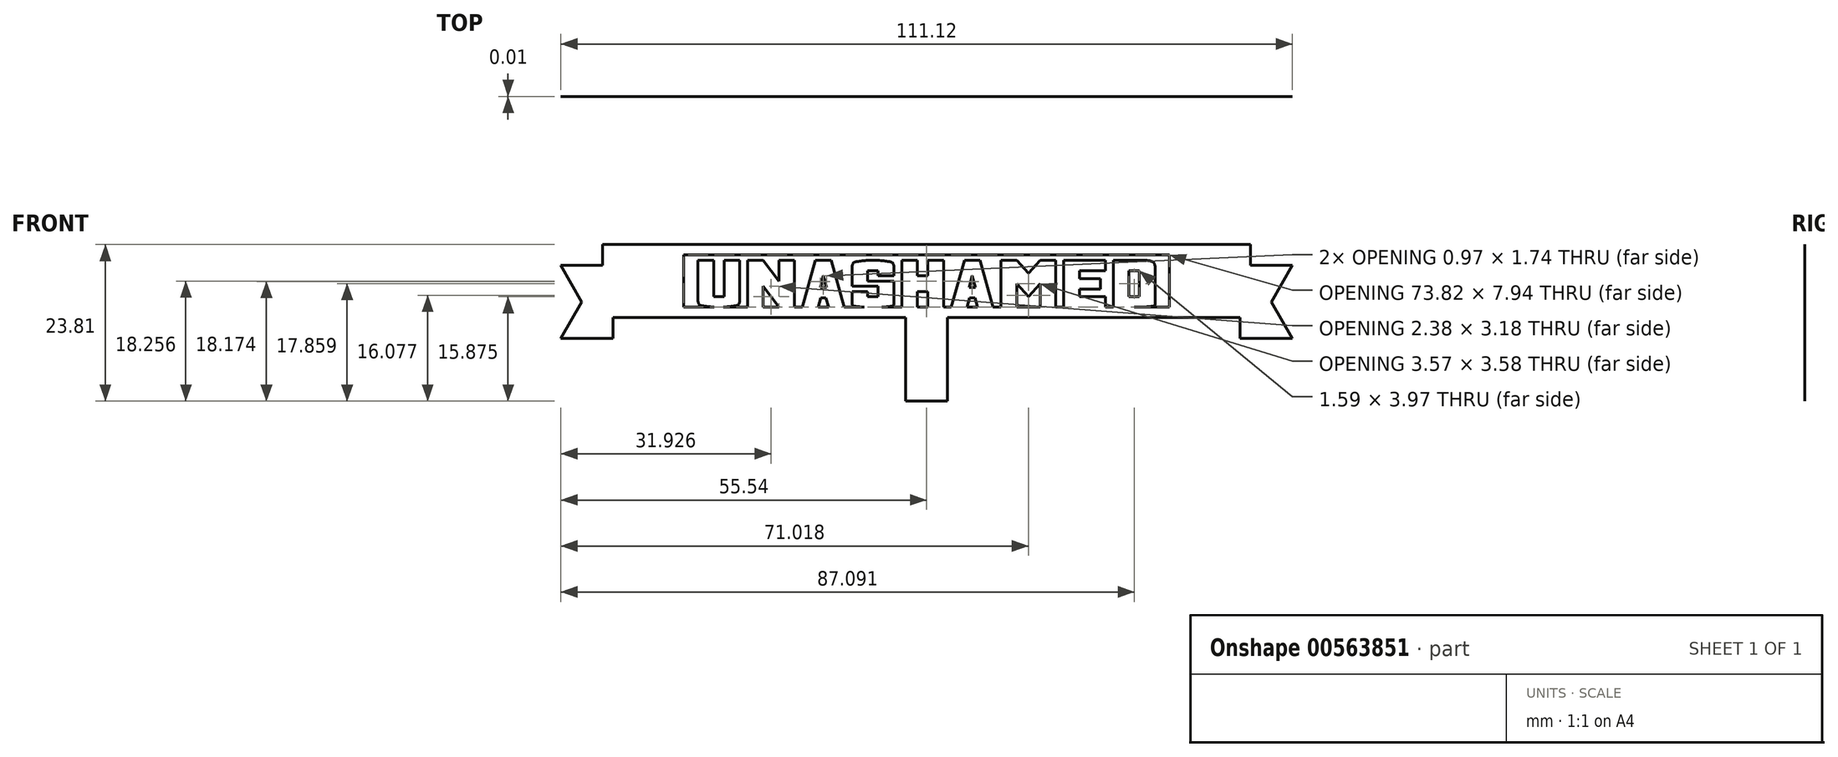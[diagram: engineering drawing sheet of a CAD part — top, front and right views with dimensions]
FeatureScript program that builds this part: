
annotation { "Feature Type Name" : "Feature", "Feature Type Description" : "" }
export const myFeature = defineFeature(function(context is Context, id is Id, definition is map)
    precondition{}
    {
        {
            var Q0;
            Q0=qCreatedBy(makeId("Front.planeOp"),FACE);
            var sketch = newSketch(context, id + "F0", { "sketchPlane" : qUnion([Q0])});
            skLineSegment(sketch, "E0.bottom", {"start": v(55.58, 34.93) * mm, "end": v(-55.54, 34.93) * mm});
            skLineSegment(sketch, "E0.top", {"start": v(55.58, -34.92) * mm, "end": v(-55.54, -34.93) * mm});
            skLineSegment(sketch, "E0.left", {"start": v(55.58, 34.93) * mm, "end": v(55.58, -34.92) * mm});
            skLineSegment(sketch, "E0.right", {"start": v(-55.54, 34.93) * mm, "end": v(-55.54, -34.93) * mm});
            skLineSegment(sketch, "E1", {"start": v(-47.6, -31.75) * mm, "end": v(47.64, -31.75) * mm});
            skLineSegment(sketch, "E2", {"start": v(-47.6, -31.75) * mm, "end": v(-47.6, -34.93) * mm});
            skLineSegment(sketch, "E3", {"start": v(-47.6, -34.93) * mm, "end": v(-55.54, -34.93) * mm});
            skLineSegment(sketch, "E4", {"start": v(-55.54, -34.93) * mm, "end": v(-52.37, -29.37) * mm});
            skLineSegment(sketch, "E5", {"start": v(-52.37, -29.37) * mm, "end": v(-55.54, -23.81) * mm});
            skLineSegment(sketch, "E6", {"start": v(-55.54, -23.81) * mm, "end": v(-49.2, -23.81) * mm});
            skLineSegment(sketch, "E7.bottom", {"start": v(36.9, -22.23) * mm, "end": v(-36.9, -22.23) * mm});
            skLineSegment(sketch, "E7.top", {"start": v(36.9, -30.16) * mm, "end": v(-36.9, -30.16) * mm});
            skLineSegment(sketch, "E7.left", {"start": v(36.9, -22.23) * mm, "end": v(36.9, -30.16) * mm});
            skLineSegment(sketch, "E7.right", {"start": v(-36.9, -22.22) * mm, "end": v(-36.9, -30.16) * mm});
            skPoint(sketch, "E7.middle", {"position": v(0, -26.2) * mm});
            skLineSegment(sketch, "E8", {"start": v(-34.73, -30.16) * mm, "end": v(-34.73, -23.02) * mm});
            skLineSegment(sketch, "E9", {"start": v(-34.73, -23.02) * mm, "end": v(-32.35, -23.02) * mm});
            skLineSegment(sketch, "E10", {"start": v(-32.35, -23.02) * mm, "end": v(-32.35, -28.57) * mm});
            skLineSegment(sketch, "E11", {"start": v(-30.76, -28.57) * mm, "end": v(-30.76, -23.02) * mm});
            skLineSegment(sketch, "E12", {"start": v(-30.76, -23.02) * mm, "end": v(-28.38, -23.02) * mm});
            skLineSegment(sketch, "E13", {"start": v(-28.38, -23.02) * mm, "end": v(-28.38, -30.16) * mm});
            skLineSegment(sketch, "E14", {"start": v(-28.38, -30.16) * mm, "end": v(-34.73, -30.16) * mm});
            skLineSegment(sketch, "E15", {"start": v(28.38, -30.16) * mm, "end": v(28.38, -23.02) * mm});
            skLineSegment(sketch, "E16", {"start": v(28.38, -23.02) * mm, "end": v(34.73, -23.02) * mm});
            skLineSegment(sketch, "E17", {"start": v(34.73, -23.02) * mm, "end": v(34.73, -30.16) * mm});
            skLineSegment(sketch, "E18", {"start": v(34.73, -30.16) * mm, "end": v(28.38, -30.16) * mm});
            skLineSegment(sketch, "E19", {"start": v(30.76, -28.57) * mm, "end": v(30.76, -24.6) * mm});
            skLineSegment(sketch, "E20", {"start": v(30.76, -24.6) * mm, "end": v(32.35, -24.6) * mm});
            skLineSegment(sketch, "E21", {"start": v(32.35, -24.6) * mm, "end": v(32.35, -28.57) * mm});
            skLineSegment(sketch, "E22", {"start": v(32.35, -28.58) * mm, "end": v(30.76, -28.58) * mm});
            skLineSegment(sketch, "E23", {"start": v(-49.2, -20.64) * mm, "end": v(49.23, -20.64) * mm});
            skArc(sketch, "E24", {"start": v(-48.44, 34.93) * mm, "mid": v(0, 9.84) * mm, "end": v(48.44, 34.93) * mm});
            skLineSegment(sketch, "E25", {"start": v(47.64, -31.75) * mm, "end": v(47.64, -34.92) * mm});
            skLineSegment(sketch, "E26", {"start": v(47.64, -34.92) * mm, "end": v(55.58, -34.92) * mm});
            skLineSegment(sketch, "E27", {"start": v(55.58, -34.92) * mm, "end": v(52.4, -29.37) * mm});
            skLineSegment(sketch, "E28", {"start": v(52.4, -29.37) * mm, "end": v(55.58, -23.81) * mm});
            skLineSegment(sketch, "E29", {"start": v(55.58, -23.81) * mm, "end": v(49.23, -23.81) * mm});
            skLineSegment(sketch, "E30", {"start": v(49.23, -23.82) * mm, "end": v(49.23, -23.81) * mm});
            skLineSegment(sketch, "E31", {"start": v(49.23, -23.81) * mm, "end": v(49.23, -20.64) * mm});
            skLineSegment(sketch, "E32", {"start": v(-3.16, -31.75) * mm, "end": v(-3.16, -44.45) * mm});
            skLineSegment(sketch, "E33", {"start": v(-3.16, -44.45) * mm, "end": v(3.2, -44.45) * mm});
            skLineSegment(sketch, "E34", {"start": v(3.2, -44.45) * mm, "end": v(3.2, -31.75) * mm});
            skLineSegment(sketch, "E35", {"start": v(-49.2, -23.81) * mm, "end": v(-49.2, -20.64) * mm});
            skLineSegment(sketch, "E36", {"start": v(-32.35, -28.58) * mm, "end": v(-30.76, -28.58) * mm});
            skLineSegment(sketch, "E37", {"start": v(-27.19, -30.16) * mm, "end": v(-27.19, -23.02) * mm});
            skLineSegment(sketch, "E38", {"start": v(-27.19, -23.02) * mm, "end": v(-24.8, -23.02) * mm});
            skLineSegment(sketch, "E39", {"start": v(-24.8, -23.02) * mm, "end": v(-22.42, -26.2) * mm});
            skLineSegment(sketch, "E40", {"start": v(-22.42, -26.2) * mm, "end": v(-22.42, -23.02) * mm});
            skLineSegment(sketch, "E41", {"start": v(-22.42, -23.02) * mm, "end": v(-20.04, -23.02) * mm});
            skLineSegment(sketch, "E42", {"start": v(-20.04, -23.02) * mm, "end": v(-20.04, -30.16) * mm});
            skLineSegment(sketch, "E43", {"start": v(-20.04, -30.16) * mm, "end": v(-22.42, -30.16) * mm});
            skLineSegment(sketch, "E44", {"start": v(-22.42, -30.16) * mm, "end": v(-24.8, -26.99) * mm});
            skLineSegment(sketch, "E45", {"start": v(-24.8, -26.99) * mm, "end": v(-24.8, -30.16) * mm});
            skLineSegment(sketch, "E46", {"start": v(-24.8, -30.16) * mm, "end": v(-27.19, -30.16) * mm});
            skLineSegment(sketch, "E47", {"start": v(-18.85, -30.16) * mm, "end": v(-16.87, -23.02) * mm});
            skLineSegment(sketch, "E48", {"start": v(-16.87, -23.02) * mm, "end": v(-14.49, -23.02) * mm});
            skLineSegment(sketch, "E49", {"start": v(-14.49, -23.02) * mm, "end": v(-12.5, -30.16) * mm});
            skLineSegment(sketch, "E50", {"start": v(-12.5, -30.16) * mm, "end": v(-14.88, -30.16) * mm});
            skLineSegment(sketch, "E51", {"start": v(-14.88, -30.16) * mm, "end": v(-15.28, -28.73) * mm});
            skLineSegment(sketch, "E52", {"start": v(-15.28, -28.73) * mm, "end": v(-16.07, -28.73) * mm});
            skLineSegment(sketch, "E53", {"start": v(-16.07, -28.73) * mm, "end": v(-16.47, -30.16) * mm});
            skLineSegment(sketch, "E54", {"start": v(-16.47, -30.16) * mm, "end": v(-18.85, -30.16) * mm});
            skPoint(sketch, "E55", {"position": v(-15.68, -23.02) * mm});
            skLineSegment(sketch, "E56", {"start": v(-15.68, -25.4) * mm, "end": v(-16.16, -27.15) * mm});
            skLineSegment(sketch, "E57", {"start": v(-16.16, -27.15) * mm, "end": v(-15.2, -27.15) * mm});
            skLineSegment(sketch, "E58", {"start": v(-15.2, -27.15) * mm, "end": v(-15.68, -25.4) * mm});
            skLineSegment(sketch, "E59", {"start": v(-3.77, -30.16) * mm, "end": v(-3.77, -23.02) * mm});
            skLineSegment(sketch, "E60", {"start": v(-3.77, -23.02) * mm, "end": v(-1.39, -23.02) * mm});
            skLineSegment(sketch, "E61", {"start": v(-1.39, -23.02) * mm, "end": v(-1.39, -25.4) * mm});
            skLineSegment(sketch, "E62", {"start": v(-1.39, -25.4) * mm, "end": v(0.2, -25.4) * mm});
            skLineSegment(sketch, "E63", {"start": v(0.2, -25.4) * mm, "end": v(0.2, -23.02) * mm});
            skLineSegment(sketch, "E64", {"start": v(0.2, -23.02) * mm, "end": v(2.58, -23.02) * mm});
            skLineSegment(sketch, "E65", {"start": v(2.58, -23.02) * mm, "end": v(2.58, -30.16) * mm});
            skLineSegment(sketch, "E66", {"start": v(2.58, -30.16) * mm, "end": v(0.2, -30.16) * mm});
            skLineSegment(sketch, "E67", {"start": v(0.2, -30.16) * mm, "end": v(0.2, -27.78) * mm});
            skLineSegment(sketch, "E68", {"start": v(0.2, -27.78) * mm, "end": v(-1.39, -27.78) * mm});
            skLineSegment(sketch, "E69", {"start": v(-1.39, -27.78) * mm, "end": v(-1.39, -30.16) * mm});
            skLineSegment(sketch, "E70", {"start": v(-1.39, -30.16) * mm, "end": v(-3.77, -30.16) * mm});
            skLineSegment(sketch, "E71", {"start": v(3.77, -30.16) * mm, "end": v(5.75, -23.02) * mm});
            skLineSegment(sketch, "E72", {"start": v(5.75, -23.02) * mm, "end": v(8.14, -23.02) * mm});
            skLineSegment(sketch, "E73", {"start": v(8.14, -23.02) * mm, "end": v(10.12, -30.16) * mm});
            skLineSegment(sketch, "E74", {"start": v(10.12, -30.16) * mm, "end": v(7.74, -30.16) * mm});
            skLineSegment(sketch, "E75", {"start": v(7.74, -30.16) * mm, "end": v(7.34, -28.73) * mm});
            skLineSegment(sketch, "E76", {"start": v(7.34, -28.73) * mm, "end": v(6.55, -28.73) * mm});
            skLineSegment(sketch, "E77", {"start": v(6.55, -28.73) * mm, "end": v(6.15, -30.16) * mm});
            skLineSegment(sketch, "E78", {"start": v(6.15, -30.16) * mm, "end": v(3.77, -30.16) * mm});
            skPoint(sketch, "E79", {"position": v(6.95, -23.02) * mm});
            skLineSegment(sketch, "E80", {"start": v(6.95, -25.4) * mm, "end": v(6.46, -27.15) * mm});
            skLineSegment(sketch, "E81", {"start": v(6.46, -27.15) * mm, "end": v(7.43, -27.15) * mm});
            skLineSegment(sketch, "E82", {"start": v(7.43, -27.15) * mm, "end": v(6.95, -25.4) * mm});
            skLineSegment(sketch, "E83", {"start": v(11.31, -30.16) * mm, "end": v(11.31, -23.02) * mm});
            skLineSegment(sketch, "E84", {"start": v(11.31, -23.02) * mm, "end": v(13.7, -23.02) * mm});
            skLineSegment(sketch, "E85", {"start": v(13.7, -23.02) * mm, "end": v(15.48, -25) * mm});
            skLineSegment(sketch, "E86", {"start": v(15.48, -25) * mm, "end": v(17.26, -23.02) * mm});
            skLineSegment(sketch, "E87", {"start": v(17.26, -23.02) * mm, "end": v(19.65, -23.02) * mm});
            skLineSegment(sketch, "E88", {"start": v(19.65, -23.02) * mm, "end": v(19.65, -30.16) * mm});
            skLineSegment(sketch, "E89", {"start": v(19.65, -30.16) * mm, "end": v(17.26, -30.16) * mm});
            skLineSegment(sketch, "E90", {"start": v(17.26, -30.16) * mm, "end": v(17.26, -26.58) * mm});
            skLineSegment(sketch, "E91", {"start": v(15.48, -28.57) * mm, "end": v(17.26, -26.58) * mm});
            skLineSegment(sketch, "E92", {"start": v(15.48, -28.58) * mm, "end": v(13.7, -26.58) * mm});
            skLineSegment(sketch, "E93", {"start": v(13.7, -26.58) * mm, "end": v(13.7, -30.16) * mm});
            skLineSegment(sketch, "E94", {"start": v(13.7, -30.16) * mm, "end": v(11.31, -30.16) * mm});
            skLineSegment(sketch, "E95", {"start": v(20.84, -23.02) * mm, "end": v(20.84, -30.16) * mm});
            skLineSegment(sketch, "E96", {"start": v(20.84, -30.16) * mm, "end": v(27.19, -30.16) * mm});
            skLineSegment(sketch, "E97", {"start": v(27.19, -30.16) * mm, "end": v(27.19, -28.58) * mm});
            skLineSegment(sketch, "E98", {"start": v(27.19, -28.58) * mm, "end": v(23.22, -28.58) * mm});
            skLineSegment(sketch, "E99", {"start": v(23.22, -28.58) * mm, "end": v(23.22, -27.38) * mm});
            skLineSegment(sketch, "E100", {"start": v(23.22, -27.38) * mm, "end": v(26.4, -27.38) * mm});
            skLineSegment(sketch, "E101", {"start": v(26.4, -27.38) * mm, "end": v(26.4, -25.8) * mm});
            skLineSegment(sketch, "E102", {"start": v(26.4, -25.8) * mm, "end": v(23.22, -25.8) * mm});
            skLineSegment(sketch, "E103", {"start": v(23.22, -25.8) * mm, "end": v(23.22, -24.6) * mm});
            skLineSegment(sketch, "E104", {"start": v(23.22, -24.6) * mm, "end": v(27.19, -24.6) * mm});
            skLineSegment(sketch, "E105", {"start": v(27.19, -24.6) * mm, "end": v(27.19, -23.02) * mm});
            skLineSegment(sketch, "E106", {"start": v(27.19, -23.02) * mm, "end": v(20.84, -23.02) * mm});
            skPoint(sketch, "E107", {"position": v(31.55, -23.02) * mm});
            skLineSegment(sketch, "E108", {"start": v(-4.96, -23.02) * mm, "end": v(-4.96, -25.4) * mm});
            skLineSegment(sketch, "E109", {"start": v(-4.96, -25.4) * mm, "end": v(-7.34, -25.4) * mm});
            skLineSegment(sketch, "E110", {"start": v(-7.34, -25.4) * mm, "end": v(-7.34, -24.6) * mm});
            skLineSegment(sketch, "E111", {"start": v(-7.34, -24.6) * mm, "end": v(-8.93, -24.6) * mm});
            skLineSegment(sketch, "E112", {"start": v(-8.93, -24.6) * mm, "end": v(-8.93, -26.2) * mm});
            skLineSegment(sketch, "E113", {"start": v(-8.93, -26.2) * mm, "end": v(-4.96, -26.2) * mm});
            skLineSegment(sketch, "E114", {"start": v(-4.96, -26.2) * mm, "end": v(-4.96, -30.16) * mm});
            skLineSegment(sketch, "E115", {"start": v(-4.96, -30.16) * mm, "end": v(-11.31, -30.16) * mm});
            skLineSegment(sketch, "E116", {"start": v(-11.31, -30.16) * mm, "end": v(-11.31, -27.78) * mm});
            skLineSegment(sketch, "E117", {"start": v(-11.31, -27.78) * mm, "end": v(-8.93, -27.78) * mm});
            skLineSegment(sketch, "E118", {"start": v(-8.93, -27.78) * mm, "end": v(-8.93, -28.57) * mm});
            skLineSegment(sketch, "E119", {"start": v(-8.93, -28.58) * mm, "end": v(-7.34, -28.58) * mm});
            skLineSegment(sketch, "E120", {"start": v(-7.34, -28.57) * mm, "end": v(-7.34, -26.99) * mm});
            skLineSegment(sketch, "E121", {"start": v(-7.34, -26.99) * mm, "end": v(-11.31, -26.99) * mm});
            skLineSegment(sketch, "E122", {"start": v(-11.31, -26.99) * mm, "end": v(-11.31, -23.02) * mm});
            skLineSegment(sketch, "E123", {"start": v(-11.31, -23.02) * mm, "end": v(-4.96, -23.02) * mm});
            skFitSpline(sketch, "E124", {"points": [v(-11.31, -24.2) * mm, v(-11.11, -23.42) * mm, v(-10.52, -23.22) * mm, v(-8.14, -23.02) * mm, v(-5.75, -23.22) * mm, v(-5.16, -23.42) * mm, v(-4.96, -24.2) * mm], "startDerivative": vector(0, 8.54) * mm, "endDerivative": vector(0, -8.54) * mm});
            skFitSpline(sketch, "E125", {"points": [v(-11.31, -28.97) * mm, v(-11.31, -29.77) * mm, v(-11.11, -29.96) * mm, v(-8.14, -30.19) * mm, v(-5.16, -29.96) * mm, v(-4.96, -29.77) * mm, v(-4.96, -28.97) * mm], "startDerivative": vector(0, -8.41) * mm, "endDerivative": vector(0, 8.41) * mm});
            skFitSpline(sketch, "E126", {"points": [v(-34.73, -28.97) * mm, v(-34.53, -29.77) * mm, v(-33.93, -29.96) * mm, v(-31.55, -30.19) * mm, v(-29.17, -29.96) * mm, v(-28.58, -29.77) * mm, v(-28.38, -28.97) * mm], "startDerivative": vector(0, -8.54) * mm, "endDerivative": vector(0, 8.54) * mm});
            skFitSpline(sketch, "E127", {"points": [v(31.55, -30.16) * mm, v(34.53, -29.96) * mm, v(34.73, -29.77) * mm, v(34.73, -28.97) * mm], "startDerivative": vector(6.5, 0.02) * mm, "endDerivative": vector(0, 4.2) * mm});
            skFitSpline(sketch, "E128", {"points": [v(31.55, -23.02) * mm, v(33.93, -23.12) * mm, v(34.53, -23.42) * mm, v(34.73, -24.2) * mm], "startDerivative": vector(7.55, 0) * mm, "endDerivative": vector(0, -4.3) * mm});
            skLineSegment(sketch, "E129", {"start": v(-31.55, -30.16) * mm, "end": v(-31.55, -30.19) * mm});
            skLineSegment(sketch, "E130", {"start": v(-8.14, -30.16) * mm, "end": v(-8.14, -30.19) * mm});
            skSolve(sketch);
        }
        {
            var Q0;
            {var subQ0=sQuery(id+"F0.wireOp",EDGE,"E9");Q0=makeQuery(id+"F0.imprint","IMPRINT",FACE,{"disambiguationData":[TD([[makeQuery(id+"F0.imprint","IMPRINT",EDGE,{"derivedFrom":subQ0}),-1.0]])]});}
            var Q1;
            Q1=makeQuery(id+"F0.imprint","IMPRINT",FACE,{"disambiguationData":[TD([[makeQuery(id+"F0.imprint","IMPRINT",EDGE,{"derivedFrom":sQuery(id+"F0.wireOp",EDGE,"E37")}),-1.0]])]});
            var Q2;
            {var subQ21=sQuery(id+"F0.wireOp",EDGE,"E2");Q2=makeQuery(id+"F0.imprint","IMPRINT",FACE,{"disambiguationData":[TD([[makeQuery(id+"F0.imprint","IMPRINT",EDGE,{"derivedFrom":subQ21}),-1.0]])]});}
            var Q3;
            Q3=makeQuery(id+"F0.imprint","IMPRINT",FACE,{"disambiguationData":[TD([[makeQuery(id+"F0.imprint","IMPRINT",EDGE,{"derivedFrom":sQuery(id+"F0.wireOp",EDGE,"E47")}),-1.0]])]});
            var Q4;
            {var subQ5=sQuery(id+"F0.wireOp",EDGE,"E33");Q4=makeQuery(id+"F0.imprint","IMPRINT",FACE,{"disambiguationData":[TD([[makeQuery(id+"F0.imprint","IMPRINT",EDGE,{"derivedFrom":subQ5}),1.0]])]});}
            var Q5;
            {var subQ0=sQuery(id+"F0.wireOp",EDGE,"E34");var subQ1=sQuery(id+"F0.wireOp",EDGE,"E0.top");var subQ2=makeQuery(id+"F0.imprint","INTERSECT",VERTEX,{"derivedFrom":[subQ1,subQ0]});Q5=makeQuery(id+"F0.imprint","IMPRINT",FACE,{"disambiguationData":[TD([[makeQuery(id+"F0.imprint","IMPRINT",EDGE,{"disambiguationData":[TD([[subQ2,-1.0]])],"derivedFrom":subQ1}),-1.0]])]});}
            var Q6;
            Q6=makeQuery(id+"F0.imprint","IMPRINT",FACE,{"disambiguationData":[TD([[makeQuery(id+"F0.imprint","IMPRINT",EDGE,{"derivedFrom":sQuery(id+"F0.wireOp",EDGE,"E71")}),-1.0]])]});
            var Q7;
            Q7=makeQuery(id+"F0.imprint","IMPRINT",FACE,{"disambiguationData":[TD([[makeQuery(id+"F0.imprint","IMPRINT",EDGE,{"derivedFrom":sQuery(id+"F0.wireOp",EDGE,"E83")}),-1.0]])]});
            var Q8;
            Q8=makeQuery(id+"F0.imprint","IMPRINT",FACE,{"disambiguationData":[TD([[makeQuery(id+"F0.imprint","IMPRINT",EDGE,{"derivedFrom":sQuery(id+"F0.wireOp",EDGE,"E95")}),1.0]])]});
            var Q9;
            Q9=makeQuery(id+"F0.imprint","IMPRINT",FACE,{"disambiguationData":[TD([[makeQuery(id+"F0.imprint","IMPRINT",EDGE,{"derivedFrom":sQuery(id+"F0.wireOp",EDGE,"E59")}),-1.0]])]});
            var Q10;
            {var subQ6=sQuery(id+"F0.wireOp",EDGE,"E109");Q10=makeQuery(id+"F0.imprint","IMPRINT",FACE,{"disambiguationData":[TD([[makeQuery(id+"F0.imprint","IMPRINT",EDGE,{"derivedFrom":subQ6}),-1.0]])]});}
            var Q11;
            {var subQ5=sQuery(id+"F0.wireOp",EDGE,"E15");Q11=makeQuery(id+"F0.imprint","IMPRINT",FACE,{"disambiguationData":[TD([[makeQuery(id+"F0.imprint","IMPRINT",EDGE,{"derivedFrom":subQ5}),-1.0]])]});}
            var Q12;
            {var subQ0=sQuery(id+"F0.wireOp",EDGE,"E130");Q12=makeQuery(id+"F0.imprint","IMPRINT",FACE,{"disambiguationData":[TD([[makeQuery(id+"F0.imprint","IMPRINT",EDGE,{"derivedFrom":subQ0}),-1.0]])]});}
            var Q13;
            {var subQ0=sQuery(id+"F0.wireOp",EDGE,"E130");Q13=makeQuery(id+"F0.imprint","IMPRINT",FACE,{"disambiguationData":[TD([[makeQuery(id+"F0.imprint","IMPRINT",EDGE,{"derivedFrom":subQ0}),1.0]])]});}
            var Q14;
            {var subQ0=sQuery(id+"F0.wireOp",EDGE,"E129");Q14=makeQuery(id+"F0.imprint","IMPRINT",FACE,{"disambiguationData":[TD([[makeQuery(id+"F0.imprint","IMPRINT",EDGE,{"derivedFrom":subQ0}),-1.0]])]});}
            var Q15;
            {var subQ0=sQuery(id+"F0.wireOp",EDGE,"E129");Q15=makeQuery(id+"F0.imprint","IMPRINT",FACE,{"disambiguationData":[TD([[makeQuery(id+"F0.imprint","IMPRINT",EDGE,{"derivedFrom":subQ0}),1.0]])]});}
            extrude(context, id + "F1", {"entities" : qUnion([Q0, Q1, Q2, Q3, Q4, Q5, Q6, Q7, Q8, Q9, Q10, Q11, Q12, Q13, Q14, Q15]), "depth" : 1 / 101.6 * mm, "offsetDistance" : 25.4 * mm});
        }
    });
